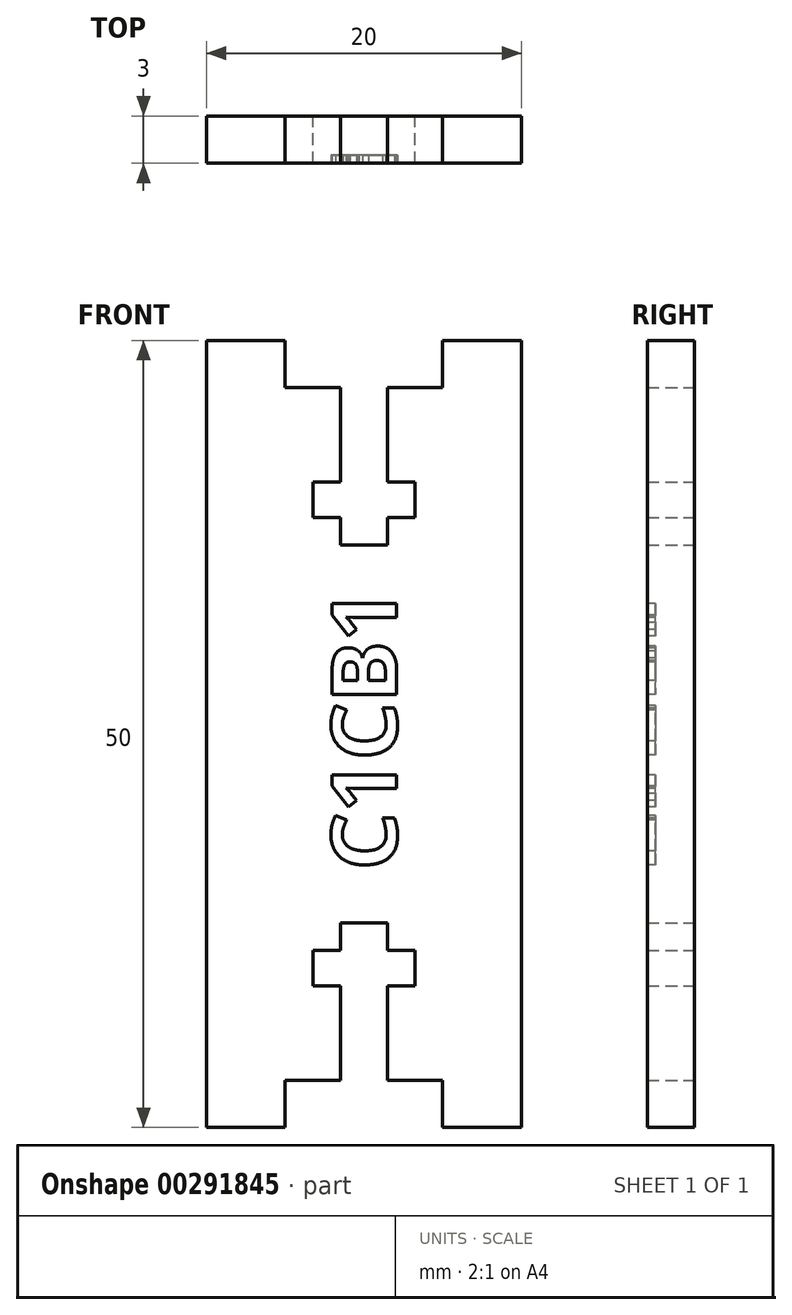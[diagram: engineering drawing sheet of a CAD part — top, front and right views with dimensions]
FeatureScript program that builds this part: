
annotation { "Feature Type Name" : "Feature", "Feature Type Description" : "" }
export const myFeature = defineFeature(function(context is Context, id is Id, definition is map)
    precondition{}
    {
        {
            assignVariable(context, id + "F0", {"name" : "material_thickness", "anyValue" : 3});
        }
        {
            var Q0;
            Q0=qCreatedBy(makeId("Front.planeOp"),FACE);
            var sketch = newSketch(context, id + "F1", { "sketchPlane" : qUnion([Q0])});
            skLineSegment(sketch, "E0", {"start": v(-10, 25) * mm, "end": v(-5, 25) * mm});
            skLineSegment(sketch, "E1", {"start": v(-5, 25) * mm, "end": v(-5, 22) * mm});
            skLineSegment(sketch, "E2", {"start": v(-5, 22) * mm, "end": v(-1.5, 22) * mm});
            skLineSegment(sketch, "E3", {"start": v(-1.5, 22) * mm, "end": v(-1.5, 16) * mm});
            skLineSegment(sketch, "E4", {"start": v(-1.5, 16) * mm, "end": v(-3.25, 16) * mm});
            skLineSegment(sketch, "E5", {"start": v(-3.25, 16) * mm, "end": v(-3.25, 13.75) * mm});
            skLineSegment(sketch, "E6", {"start": v(-3.25, 13.75) * mm, "end": v(-1.5, 13.75) * mm});
            skLineSegment(sketch, "E7", {"start": v(-1.5, 13.75) * mm, "end": v(-1.5, 12) * mm});
            skLineSegment(sketch, "E8", {"start": v(-1.5, 12) * mm, "end": v(0, 12) * mm});
            skLineSegment(sketch, "E9", {"start": v(0, 12) * mm, "end": v(0, 0) * mm});
            skLineSegment(sketch, "E10", {"start": v(0, 0) * mm, "end": v(-10, 0) * mm});
            skLineSegment(sketch, "E11", {"start": v(-10, 0) * mm, "end": v(-10, 25) * mm});
            skSolve(sketch);
        }
        {
            var Q0;
            Q0=makeQuery(id+"F1.imprint","IMPRINT",FACE,{"disambiguationData":[TD([[makeQuery(id+"F1.imprint","IMPRINT",EDGE,{"derivedFrom":sQuery(id+"F1.wireOp",EDGE,"E0")}),-1.0]])]});
            extrude(context, id + "F2", {"entities" : qUnion([Q0]), "depth" : (getVariable(context, 'material_thickness')) * mm});
        }
        {
            var Q0;
            Q0=makeQuery(id+"F2.opExtrude","SWEPT_BODY",BODY,{"disambiguationData":[OSD([sQuery(id+"F1.wireOp",EDGE,"E0"),sQuery(id+"F1.wireOp",EDGE,"E1"),sQuery(id+"F1.wireOp",EDGE,"E2"),sQuery(id+"F1.wireOp",EDGE,"E3"),sQuery(id+"F1.wireOp",EDGE,"E4"),sQuery(id+"F1.wireOp",EDGE,"E5"),sQuery(id+"F1.wireOp",EDGE,"E6"),sQuery(id+"F1.wireOp",EDGE,"E7"),sQuery(id+"F1.wireOp",EDGE,"E8"),sQuery(id+"F1.wireOp",EDGE,"E9"),sQuery(id+"F1.wireOp",EDGE,"E11"),sQuery(id+"F1.wireOp",EDGE,"E10")])]});
            var Q1;
            Q1=qCreatedBy(makeId("Right.planeOp"),FACE);
            mirror(context, id + "F3", {"operationType" : NewBodyOperationType.ADD, "entities" : qUnion([Q0]), "mirrorPlane" : qUnion([Q1])});
        }
        {
            var Q0;
            Q0=makeQuery(id+"F2.opExtrude","SWEPT_BODY",BODY,{"disambiguationData":[OSD([sQuery(id+"F1.wireOp",EDGE,"E0"),sQuery(id+"F1.wireOp",EDGE,"E1"),sQuery(id+"F1.wireOp",EDGE,"E2"),sQuery(id+"F1.wireOp",EDGE,"E3"),sQuery(id+"F1.wireOp",EDGE,"E4"),sQuery(id+"F1.wireOp",EDGE,"E5"),sQuery(id+"F1.wireOp",EDGE,"E6"),sQuery(id+"F1.wireOp",EDGE,"E7"),sQuery(id+"F1.wireOp",EDGE,"E8"),sQuery(id+"F1.wireOp",EDGE,"E9"),sQuery(id+"F1.wireOp",EDGE,"E11"),sQuery(id+"F1.wireOp",EDGE,"E10")])]});
            var Q1;
            Q1=qCreatedBy(makeId("Top.planeOp"),FACE);
            mirror(context, id + "F4", {"operationType" : NewBodyOperationType.ADD, "entities" : qUnion([Q0]), "mirrorPlane" : qUnion([Q1])});
        }
        {
            var Q0;
            {var subQ0=makeQuery(id+"F2.opExtrude","CAP_FACE",FACE,{"disambiguationData":[OSD([sQuery(id+"F1.wireOp",EDGE,"E0"),sQuery(id+"F1.wireOp",EDGE,"E1"),sQuery(id+"F1.wireOp",EDGE,"E2"),sQuery(id+"F1.wireOp",EDGE,"E3"),sQuery(id+"F1.wireOp",EDGE,"E4"),sQuery(id+"F1.wireOp",EDGE,"E5"),sQuery(id+"F1.wireOp",EDGE,"E6"),sQuery(id+"F1.wireOp",EDGE,"E7"),sQuery(id+"F1.wireOp",EDGE,"E8"),sQuery(id+"F1.wireOp",EDGE,"E9"),sQuery(id+"F1.wireOp",EDGE,"E11"),sQuery(id+"F1.wireOp",EDGE,"E10")])],"isStart":false});var subQ1=makeQuery(id+"F3.boolean.opBoolean","MERGE",FACE,{"derivedFrom":[subQ0,makeQuery(id+"F3.opPattern","COPY",FACE,{"derivedFrom":subQ0,"instanceName":"1"})]});Q0=makeQuery(id+"F4.boolean.opBoolean","MERGE",FACE,{"derivedFrom":[subQ1,makeQuery(id+"F4.opPattern","COPY",FACE,{"derivedFrom":subQ1,"instanceName":"1"})]});}
            var sketch = newSketch(context, id + "F5", { "sketchPlane" : qUnion([Q0])});
            skText(sketch, "E12", { "text": "C1CB1", "fontName": "OpenSans-Bold.ttf"});
            const initialGuessF5  = {"E12": [0.00208, -0.00866, 0, 1, 0.00416]};
            skSetInitialGuess(sketch, initialGuessF5);
            skSolve(sketch);
        }
        {
            var Q0;
            Q0 = qSketchRegion(id + "F5", true);
            extrude(context, id + "F6", {"entities" : qUnion([Q0]), "operationType" : NewBodyOperationType.REMOVE, "oppositeDirection" : true, "depth" : 0.5 * mm});
        }
    });
